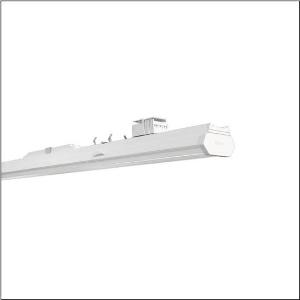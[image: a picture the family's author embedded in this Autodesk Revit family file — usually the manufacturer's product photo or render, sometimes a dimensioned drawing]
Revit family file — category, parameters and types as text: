
# Revit family: licross_r__11_protected_ho_51tp12dn4fxm_edee
name_source: partatom
category: Lighting Fixtures
units: mm (PartAtom-declared; Revit-internal decimal feet)

## family parameters
Cut with Voids When Loaded = No
Host = Face
Light Source = No
Part Type = Normal
Room Calculation Point = No
Round Connector Dimension = Use Diameter
Shared = No

## types (1)
- --- (1 x LED, 15270 lm, 87.3 W, 4000K)
    Apparent Load = 87 VA
    CIE Flux Codes = 70 91 97 98 100
    Color Rendering = 80
    Color Temperature = 4000K
    Default Elevation = 1800 mm
    Description = Licross® 11 Protected HO, luminaire insert, of sheet steel, galvanised, coil coated, white, length: 1.500mm, width: 90mm, height: 101mm, LED rated luminous flux: 15.270lm, light colour: 840, control gear: DALI 2, with plug, 5-pole, with phase selection, mains connection: 220..240V, AC, 50/60Hz, rated input power: 87W, halogen-free wiring, primary optical cover: cover, of PMMA, light emission: direct distribution, primary light characteristic: symmetric, protection rating (complete): IP64, insulation class (complete): insulation class I (protective earthing), certification: CE, ENEC, VDE, UKCA, protection symbol: D if used in an environment with conductive dust loads with corresponding accessories, impact resistance: IK06, permissible ambient temperature for indoor applications: -25..+30°C, corresponds to IFS (International Featured Standards) requirements for safety and quality in the food industry, reducing of maximum allowable ambient temperature of 5°C with ceiling mounting, LABS conformity tested according to VDMA 24364:2018-05, packaging unit: 1 piece
    Height = 92 mm
    Lamp = 1 x LED
    Lamp Light Flux = 15270 lm
    Lamp Power = 87.3 W
    Lamp count = 1
    Length = 1500 mm
    Luminous efficacy = 175 lm/W
    Manufacturer = Siteco
    ModVariant = No
    Model = 51TP12DN4FXM
    Mounting Place = Ceiling
    Mounting Type = Pendant
    Number of Poles = 1
    OnlyDefault = Yes
    Power Factor = 1
    Product Name = Licross® 11 Protected HO
    Product group = luminaire insert
    ProductGroupID = 901
    Protection Class = Protection class I
    Protection Degree = IP 64
    RLX_Detail_Level = 1
    RLX_Emergency_Light_Flux = 0 lm
    RLX_Emergency_Type = 0
    RLX_Emergency_Type_DB = No
    RlxData = <blob elided: 24381 chars, md5=4e259f91>
    Socket = socket
    Standby Power = 0 W
    System Light Flux = 15270 lm
    System Power = 87 W
    Type Comments = factory setting: luminous flux: 100 % | dim-lin: 254 | 491 mA
    Type Image = l_1256148.jpg
    URL = http://relux.com
    VarID = @adj_051979
    Voltage = 0 V
    Weight = 0.00 kg
    Width = 88 mm

## geometry (parser evidence)
native form markers: Blend x4, Sweep x10
no freeform markers — native parametric forms only
